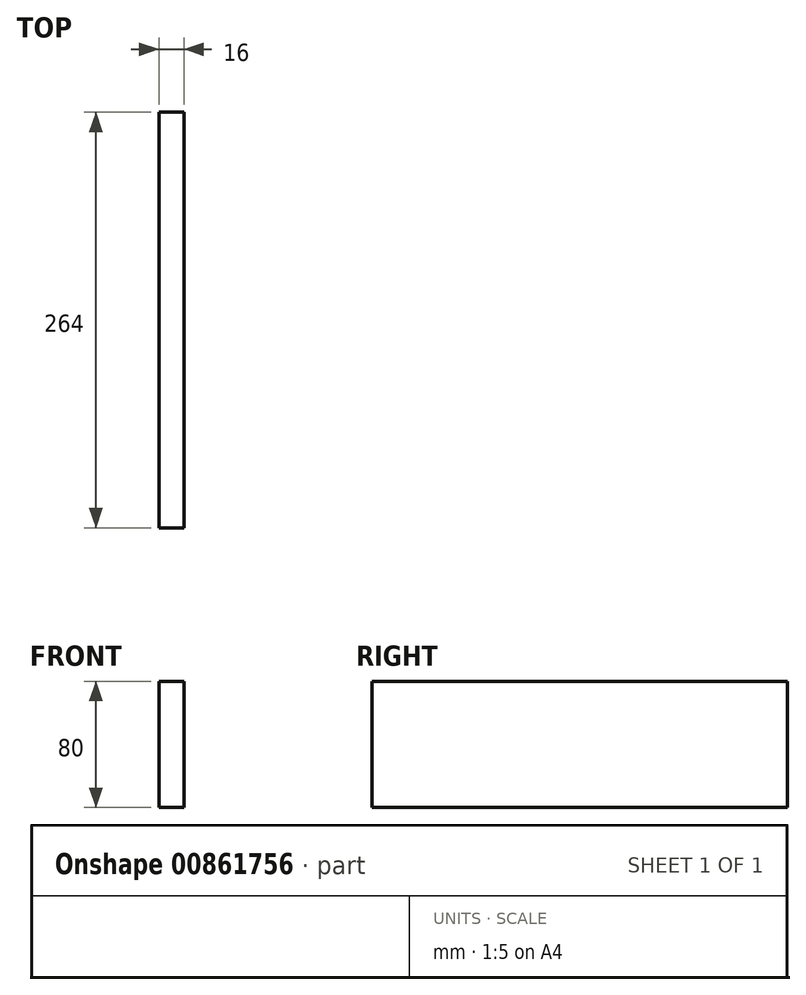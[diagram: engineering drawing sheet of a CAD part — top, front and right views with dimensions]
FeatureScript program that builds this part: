
annotation { "Feature Type Name" : "Feature", "Feature Type Description" : "" }
export const myFeature = defineFeature(function(context is Context, id is Id, definition is map)
    precondition{}
    {
        {
            var Q0;
            Q0=qCreatedBy(makeId("Front.planeOp"),FACE);
            var sketch = newSketch(context, id + "F0", { "sketchPlane" : qUnion([Q0])});
            skLineSegment(sketch, "E0.bottom", {"start": v(-192.83, 45.58) * mm, "end": v(71.17, 45.58) * mm});
            skLineSegment(sketch, "E0.top", {"start": v(-192.83, -34.42) * mm, "end": v(71.17, -34.42) * mm});
            skLineSegment(sketch, "E0.left", {"start": v(-192.83, 45.58) * mm, "end": v(-192.83, -34.42) * mm});
            skLineSegment(sketch, "E0.right", {"start": v(71.17, 45.58) * mm, "end": v(71.17, -34.42) * mm});
            skSolve(sketch);
        }
        {
            var Q0;
            Q0=makeQuery(id+"F0.imprint","IMPRINT",FACE,{"disambiguationData":[TD([[makeQuery(id+"F0.imprint","IMPRINT",EDGE,{"derivedFrom":sQuery(id+"F0.wireOp",EDGE,"E0.bottom")}),-1.0]])]});
            extrude(context, id + "F1", {"entities" : qUnion([Q0]), "depth" : 16 * mm, "offsetDistance" : 25 * mm});
        }
        {
            var Q0;
            Q0=makeQuery(id+"F1.opExtrude","SWEPT_BODY",BODY,{"disambiguationData":[OSD([sQuery(id+"F0.wireOp",EDGE,"E0.bottom"),sQuery(id+"F0.wireOp",EDGE,"E0.top"),sQuery(id+"F0.wireOp",EDGE,"E0.left"),sQuery(id+"F0.wireOp",EDGE,"E0.right")])]});
            var Q1;
            Q1=makeQuery(id+"F1.opExtrude","CAP_EDGE",EDGE,{"disambiguationData":[OSD([sQuery(id+"F0.wireOp",EDGE,"E0.right")])],"isStart":true});
            transform(context, id + "F2", {"entities" : qUnion([Q0]), "transformType" : TransformType.ROTATION, "transformAxis" : qUnion([Q1]), "angle" : 90 * degree, "makeCopy" : false});
        }
    });
